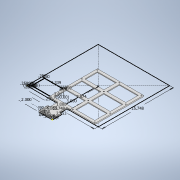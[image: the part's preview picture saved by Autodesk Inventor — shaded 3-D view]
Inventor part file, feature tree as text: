
AUTODESK INVENTOR PART (.ipt)
format: ipt  version: 2020 (Build 240168000, 168)  size: 309,248 bytes
history: native  units: in
note: dims shown in document units (in); Inventor stores cm internally (conversion verified against a paired STEP export)
features: extrude x4, sketch x3, hole x2, pattern_linear x1
ambient origin geometry x8: Origin, YZ Plane, XZ Plane, XY Plane, X Axis, Y Axis, Z Axis, Center Point
bodies: Solid1 (feature_tree)
feature tree (10):
  sketch  "Sketch1"  dims[d0=3.0in d1=2.0in]
  extrude  "Extrusion1"  Depth=2.0in
  hole  "Hole1"  [1 undecoded]
  sketch  "Sketch2"  dims[d2=0.25in d3=1.0in]
  extrude  "Extrusion2"  TaperAngle=0.0deg  [1 undecoded]
  hole  "Hole2"  [1 undecoded]
  extrude  "Extrusion3"  Depth=0.5in
  pattern_linear  "Rectangular Pattern1"  Spacing1=0.25in  [1 undecoded]
  extrude  "Extrusion4"  Depth=0.25in
  sketch  "Sketch3"  dims[d4=1.0in d5=0.0in d6=0.5in d7=0.5in d8=0.25in d9=0.25in d10=2.9528in d11=90.0deg d12=2.9528in d13=1.0in d14=7.874in d15=90.0deg d16=15.748in d17=15.748in d18=0.25in d19=0.0in d20=0.26in d21=0.5in d22=0.375in d23=0.25in d24=0.5635in d25=1.0in d26=0.8108in d27=0.25in d28=90.0deg d29=0.25in d30=0.25in d31=0.25in d32=4.3386in d33=2.9134in d34=0.25in d35=0.25in d36=0.25in d37=0.25in d38=0.25in d39=0.315in d40=90.0deg d41=0.0787in d42=0.0787in d43=0.0787in d44=0.0787in d45=0.0in d46=0.0in d47=0.203in d48=0.625in d49=0.375in d50=0.25in d51=0.5635in d52=1.0in d53=0.8108in d54=0.0787in d55=0.0in d56=1.1811in d58=4.839in d59=1.5748in d61=3.423in d62=0.25in d63=0.25in d64=0.0in d65=0.0in d66=0.25in]
note: 4 required parameter values undecoded (feature->parameter linkage not recoverable at this tier; creation-order binding heuristic only, values carry confidence <= 0.55)
